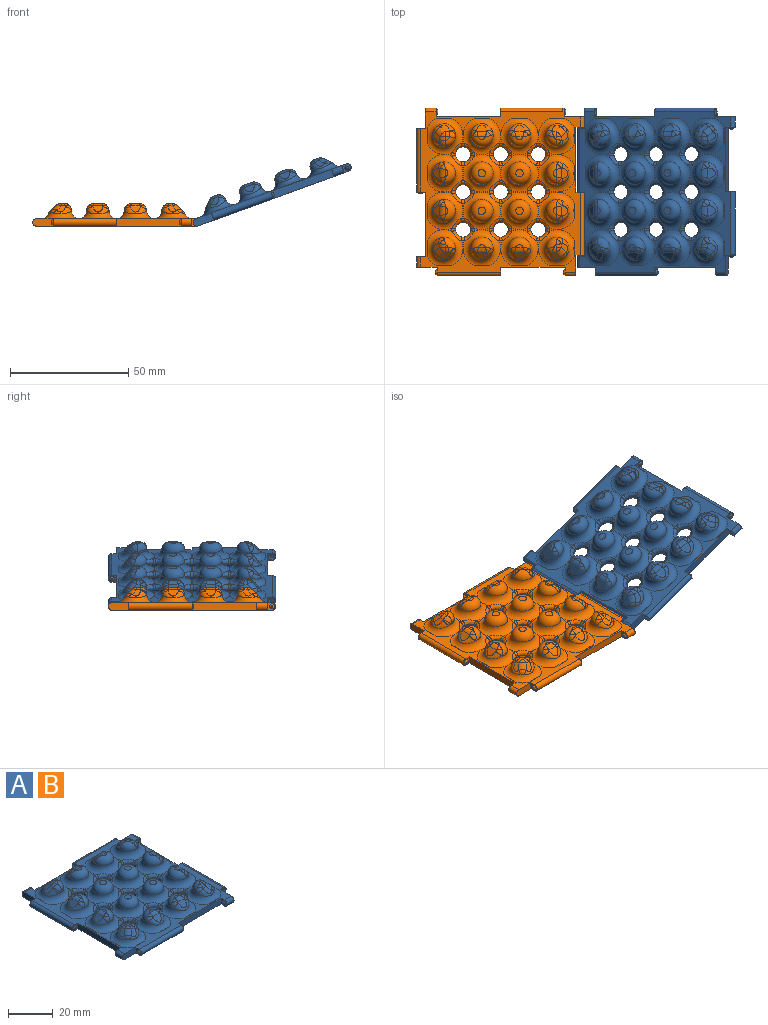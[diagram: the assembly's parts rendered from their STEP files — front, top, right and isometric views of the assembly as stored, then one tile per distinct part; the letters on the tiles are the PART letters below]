
ASSEMBLY  parts=2 mates=1
PART A: 345 faces, bbox 70.9x70.9x9.6 mm
  f0: cylinder r=3.17mm len=2.69mm, axis (0,0,-1), area 0mm2, adj f1,f344
  f1: bspline ~4.93x4.93mm, area 10.2mm2, adj f0,f2,f344
  f2: torus R=7.94mm, axis (0,0,1), area 169.6mm2, adj f1,f3,f5,f334,f335,f336,f337,f338
  f3: torus R=1.59mm, axis (0,0,1), area 113.1mm2, adj f2,f4
  f4: plane 3.18x3.18mm, normal (0,0,1), area 7.9mm2, adj f3
  f5: plane 3.22x1.37mm, normal (0,0,1), area 1.4mm2, adj f2,f6,f331
  f6: torus R=4.76mm, axis (0,0,1), area 69.6mm2, adj f5,f7,f8,f323,f324,f325,f326,f327
  f7: cylinder r=3.17mm len=2.69mm, axis (0,0,-1), area 0mm2, adj f6,f330
  f8: plane 67.68x67.68mm, normal (0,0,-1), area 3651.9mm2, adj f6,f9,f256,f259,f260,f261,f264,f265
  f9: plane 27.25x3.18mm, normal (1,0,0), area 86.5mm2, adj f8,f10,f256,f305
  f10: plane 67.68x67.68mm, normal (0,0,1), area 689.2mm2, adj f9,f11,f12,f13,f63,f64,f79,f80
  f11: plane 6.54x0.11mm, normal (0,-0.71,0.71), area 0.5mm2, adj f10,f237
  f12: plane 6.54x0.11mm, normal (0,-0.71,0.71), area 0.5mm2, adj f10,f13
  f13: torus R=7.94mm, axis (0,0,1), area 164.4mm2, adj f10,f12,f14,f47,f49,f50,f58,f59
  f14: plane 3.22x1.37mm, normal (0,0,1), area 1.4mm2, adj f13,f15,f320
  f15: torus R=7.94mm, axis (0,0,1), area 169.6mm2, adj f14,f16,f18,f36,f38,f40,f41,f42
  f16: torus R=1.59mm, axis (0,0,1), area 113.1mm2, adj f15,f17
  f17: plane 3.18x3.18mm, normal (0,0,1), area 7.9mm2, adj f16
  f18: plane 3.22x1.37mm, normal (0,0,1), area 1.4mm2, adj f15,f19,f314
  f19: torus R=7.94mm, axis (0,0,1), area 169.6mm2, adj f18,f20,f22,f23,f25,f26,f27,f29
  f20: torus R=1.59mm, axis (0,0,1), area 113.1mm2, adj f19,f21
  f21: plane 3.18x3.18mm, normal (0,0,1), area 7.9mm2, adj f20
  f22: plane 3.22x1.37mm, normal (0,0,1), area 1.4mm2, adj f19,f101,f311
  f23: bspline ~4.93x4.93mm, area 10.2mm2, adj f19,f24,f311
  f24: cylinder r=3.17mm len=2.69mm, axis (0,0,-1), area 0mm2, adj f23,f311
  f25: plane 3.22x1.37mm, normal (0,0,1), area 1.4mm2, adj f19,f311,f331
  f26: plane 3.22x1.37mm, normal (0,0,1), area 1.4mm2, adj f19,f314,f331
  f27: bspline ~4.93x4.93mm, area 10.2mm2, adj f19,f28,f314
  f28: cylinder r=3.17mm len=2.69mm, axis (0,0,-1), area 0mm2, adj f27,f314
  f29: bspline ~4.93x4.93mm, area 10.2mm2, adj f19,f30,f321
  f30: cylinder r=3.17mm len=2.69mm, axis (0,0,-1), area 0mm2, adj f29,f321
  f31: plane 3.22x1.37mm, normal (0,0,1), area 1.4mm2, adj f19,f64,f321
  f32: plane 3.22x1.37mm, normal (0,0,1), area 1.4mm2, adj f19,f64,f322
  f33: bspline ~4.93x4.93mm, area 10.2mm2, adj f19,f34,f322
  f34: cylinder r=3.17mm len=2.69mm, axis (0,0,-1), area 0mm2, adj f33,f322
  f35: plane 3.22x1.37mm, normal (0,0,1), area 1.4mm2, adj f19,f101,f322
  f36: bspline ~4.93x4.93mm, area 10.2mm2, adj f15,f37,f314
  f37: cylinder r=3.17mm len=2.69mm, axis (0,0,-1), area 0mm2, adj f36,f314
  f38: bspline ~4.93x4.93mm, area 10.2mm2, adj f15,f39,f318
  f39: cylinder r=3.17mm len=2.69mm, axis (0,0,-1), area 0mm2, adj f38,f318
  f40: plane 3.22x1.37mm, normal (0,0,1), area 1.4mm2, adj f15,f222,f318
  f41: plane 3.22x1.37mm, normal (0,0,1), area 1.4mm2, adj f15,f222,f320
  f42: bspline ~4.93x4.93mm, area 10.2mm2, adj f15,f43,f320
  f43: cylinder r=3.17mm len=2.69mm, axis (0,0,-1), area 0mm2, adj f42,f320
  f44: bspline ~4.93x4.93mm, area 10.2mm2, adj f15,f45,f321
  f45: cylinder r=3.17mm len=2.69mm, axis (0,0,-1), area 0mm2, adj f44,f321
  f46: plane 3.22x1.37mm, normal (0,0,1), area 1.4mm2, adj f15,f19,f321
  f47: bspline ~4.93x4.93mm, area 10.2mm2, adj f13,f48,f320
  f48: cylinder r=3.17mm len=2.69mm, axis (0,0,-1), area 0mm2, adj f47,f320
  f49: plane 3.22x1.37mm, normal (0,0,1), area 1.4mm2, adj f13,f237,f320
  f50: bspline ~9.97x5.14mm, area 21.5mm2, adj f13,f51,f56,f57
  f51: plane 4.37x2.65mm, normal (0,-0.71,0.71), area 12.6mm2, adj f50,f52,f56,f57
  f52: cylinder r=3.17mm len=4.07mm, axis (1,0,0), area 8.9mm2, adj f51,f53,f54,f55
  f53: bspline ~2.68x2.63mm, area 3.3mm2, adj f52,f57,f58
  f54: plane 3.06x1.16mm, normal (0,0,1), area 2.6mm2, adj f52,f58
  f55: bspline ~2.68x2.63mm, area 3.3mm2, adj f52,f56,f58
  f56: bspline ~3.74x3.12mm, area 5.3mm2, adj f50,f51,f55,f58
  f57: bspline ~3.74x3.12mm, area 5.3mm2, adj f50,f51,f53,f58
  f58: torus R=1.59mm, axis (0,0,1), area 57.5mm2, adj f13,f53,f54,f55,f56,f57
  f59: plane 3.22x1.37mm, normal (0,0,1), area 1.4mm2, adj f13,f64,f321
  f60: bspline ~4.93x4.93mm, area 10.2mm2, adj f13,f61,f321
  f61: cylinder r=3.17mm len=2.69mm, axis (0,0,-1), area 0mm2, adj f60,f321
  f62: plane 3.22x1.37mm, normal (0,0,1), area 1.4mm2, adj f13,f15,f321
  f63: plane 6.54x0.11mm, normal (0,-0.71,0.71), area 0.5mm2, adj f10,f64
  f64: torus R=7.94mm, axis (0,0,1), area 164.4mm2, adj f10,f31,f32,f59,f63,f65,f67,f75
  f65: bspline ~4.93x4.93mm, area 10.2mm2, adj f64,f66,f321
  f66: cylinder r=3.17mm len=2.69mm, axis (0,0,-1), area 0mm2, adj f65,f321
  f67: bspline ~9.7x5.14mm, area 21.5mm2, adj f64,f68,f73,f74
  f68: plane 4.37x2.65mm, normal (0,-0.71,0.71), area 12.6mm2, adj f67,f69,f73,f74
  f69: cylinder r=3.17mm len=4.07mm, axis (1,0,0), area 8.9mm2, adj f68,f70,f71,f72
  f70: bspline ~2.68x2.63mm, area 3.3mm2, adj f69,f74,f75
  f71: plane 3.06x1.16mm, normal (0,0,1), area 2.6mm2, adj f69,f75
  f72: bspline ~2.68x2.63mm, area 3.3mm2, adj f69,f73,f75
  f73: bspline ~3.74x3.12mm, area 5.3mm2, adj f67,f68,f72,f75
  f74: bspline ~3.74x3.12mm, area 5.3mm2, adj f67,f68,f70,f75
  f75: torus R=1.59mm, axis (0,0,1), area 57.5mm2, adj f64,f70,f71,f72,f73,f74
  f76: plane 3.22x1.37mm, normal (0,0,1), area 1.4mm2, adj f64,f81,f322
  f77: bspline ~4.93x4.93mm, area 10.2mm2, adj f64,f78,f322
  f78: cylinder r=3.17mm len=2.69mm, axis (0,0,-1), area 0mm2, adj f77,f322
  f79: plane 6.54x0.11mm, normal (0,-0.71,0.71), area 0.5mm2, adj f10,f81
  f80: plane 6.55x0.11mm, normal (0.71,0,0.71), area 0.5mm2, adj f10,f81
  f81: torus R=7.94mm, axis (0,0,1), area 157mm2, adj f10,f76,f79,f80,f82,f83,f85,f97
  f82: plane 3.22x1.37mm, normal (0,0,1), area 1.4mm2, adj f81,f101,f322
  f83: bspline ~4.93x4.93mm, area 10.2mm2, adj f81,f84,f322
  f84: cylinder r=3.17mm len=2.69mm, axis (0,0,-1), area 0mm2, adj f83,f322
  f85: bspline ~3.03x3.01mm, area 4.3mm2, adj f81,f86,f97,f99
  f86: cylinder r=3.17mm len=4.14mm, axis (-0.58,0.58,0.58), area 10.9mm2, adj f85,f87,f95,f96
  f87: sphere r=3.17mm, area 3.4mm2, adj f86,f88,f92
  f88: cylinder r=3.17mm len=2.25mm, axis (0,1,0), area 3.4mm2, adj f87,f89,f90,f95
  f89: plane 1.1x1.09mm, normal (0,0,1), area 0.8mm2, adj f88,f92,f98
  f90: bspline ~2.68x2.63mm, area 3.3mm2, adj f88,f91,f98
  f91: bspline ~3.74x3.12mm, area 5.3mm2, adj f90,f95,f98,f99
  f92: cylinder r=3.17mm len=2.25mm, axis (1,0,0), area 3.4mm2, adj f87,f89,f93,f96
  f93: bspline ~2.68x2.63mm, area 3.3mm2, adj f92,f94,f98
  f94: bspline ~3.74x3.12mm, area 5.3mm2, adj f93,f96,f97,f98
  f95: plane 3.65x2.65mm, normal (0.71,0,0.71), area 8.7mm2, adj f86,f88,f91,f99
  f96: plane 3.65x2.64mm, normal (0,-0.71,0.71), area 8.7mm2, adj f86,f92,f94,f97
  f97: bspline ~8.52x5.14mm, area 14.1mm2, adj f81,f85,f94,f96
  f98: torus R=1.59mm, axis (0,0,1), area 29.2mm2, adj f81,f89,f90,f91,f93,f94
  f99: bspline ~8.53x5.15mm, area 14.2mm2, adj f81,f85,f91,f95
  f100: plane 6.55x0.11mm, normal (0.71,0,0.71), area 0.5mm2, adj f10,f101
  f101: torus R=7.94mm, axis (0,0,1), area 164.4mm2, adj f10,f22,f35,f82,f100,f102,f103,f105
  f102: plane 3.22x1.37mm, normal (0,0,1), area 1.4mm2, adj f101,f117,f311
  f103: bspline ~4.93x4.93mm, area 10.2mm2, adj f101,f104,f311
  f104: cylinder r=3.17mm len=2.69mm, axis (0,0,-1), area 0mm2, adj f103,f311
  f105: bspline ~4.93x4.93mm, area 10.2mm2, adj f101,f106,f322
  f106: cylinder r=3.17mm len=2.69mm, axis (0,0,-1), area 0mm2, adj f105,f322
  f107: torus R=1.59mm, axis (0,0,1), area 57.4mm2, adj f101,f108,f111,f112,f113,f114
  f108: bspline ~2.68x2.63mm, area 3.3mm2, adj f107,f109,f111
  f109: cylinder r=3.17mm len=4.07mm, axis (0,1,0), area 8.9mm2, adj f108,f110,f113,f114
  f110: plane 4.37x2.65mm, normal (0.71,0,0.71), area 12.6mm2, adj f109,f111,f112,f115
  f111: bspline ~3.74x3.12mm, area 5.3mm2, adj f107,f108,f110,f115
  f112: bspline ~3.74x3.12mm, area 5.3mm2, adj f107,f110,f113,f115
  f113: bspline ~2.68x2.63mm, area 3.3mm2, adj f107,f109,f112
  f114: plane 3.05x1.15mm, normal (0,0,1), area 2.6mm2, adj f107,f109
  f115: bspline ~9.98x5.15mm, area 21.5mm2, adj f101,f110,f111,f112
  f116: plane 6.55x0.11mm, normal (0.71,0,0.71), area 0.5mm2, adj f10,f117
  f117: torus R=7.94mm, axis (0,0,1), area 164.4mm2, adj f10,f102,f116,f118,f119,f121,f122,f123
  f118: plane 3.22x1.37mm, normal (0,0,1), area 1.4mm2, adj f117,f136,f308
  f119: bspline ~4.93x4.93mm, area 10.2mm2, adj f117,f120,f308
  f120: cylinder r=3.17mm len=2.69mm, axis (0,0,-1), area 0mm2, adj f119,f308
  f121: plane 3.22x1.37mm, normal (0,0,1), area 1.4mm2, adj f117,f308,f331
  f122: plane 3.22x1.37mm, normal (0,0,1), area 1.4mm2, adj f117,f311,f331
  f123: bspline ~4.93x4.93mm, area 10.2mm2, adj f117,f124,f311
  f124: cylinder r=3.17mm len=2.69mm, axis (0,0,-1), area 0mm2, adj f123,f311
  f125: torus R=1.59mm, axis (0,0,1), area 57.4mm2, adj f117,f126,f129,f130,f131,f132
  f126: bspline ~2.68x2.63mm, area 3.3mm2, adj f125,f127,f129
  f127: cylinder r=3.17mm len=4.07mm, axis (0,1,0), area 8.9mm2, adj f126,f128,f131,f132
  f128: plane 4.37x2.65mm, normal (0.71,0,0.71), area 12.6mm2, adj f127,f129,f130,f133
  f129: bspline ~3.62x3.03mm, area 5.3mm2, adj f125,f126,f128,f133
  f130: bspline ~3.74x3.12mm, area 5.3mm2, adj f125,f128,f131,f133
  f131: bspline ~2.68x2.63mm, area 3.3mm2, adj f125,f127,f130
  f132: plane 3.05x1.15mm, normal (0,0,1), area 2.6mm2, adj f125,f127
  f133: bspline ~9.98x5.15mm, area 21.5mm2, adj f117,f128,f129,f130
  f134: plane 6.55x0.11mm, normal (0.71,0,0.71), area 0.5mm2, adj f10,f136
  f135: plane 6.54x0.11mm, normal (0,0.71,0.71), area 0.5mm2, adj f10,f136
  f136: torus R=7.94mm, axis (0,0,1), area 157.1mm2, adj f10,f118,f134,f135,f137,f138,f140,f152
  f137: plane 3.22x1.37mm, normal (0,0,1), area 1.4mm2, adj f136,f156,f308
  f138: bspline ~4.93x4.93mm, area 10.2mm2, adj f136,f139,f308
  f139: cylinder r=3.17mm len=2.69mm, axis (0,0,-1), area 0mm2, adj f138,f308
  f140: torus R=1.59mm, axis (0,0,1), area 29.2mm2, adj f136,f141,f148,f149,f150,f151
  f141: bspline ~3.74x3.12mm, area 5.3mm2, adj f140,f142,f148,f152
  f142: plane 3.65x2.65mm, normal (0,0.71,0.71), area 8.7mm2, adj f141,f143,f147,f152
  f143: cylinder r=3.17mm len=2.25mm, axis (-1,0,0), area 3.4mm2, adj f142,f144,f148,f149
  f144: sphere r=3.17mm, area 3.4mm2, adj f143,f145,f147
  f145: cylinder r=3.17mm len=2.25mm, axis (0,1,0), area 3.4mm2, adj f144,f146,f149,f150
  f146: plane 3.65x2.65mm, normal (0.71,0,0.71), area 8.7mm2, adj f145,f147,f151,f154
  f147: cylinder r=3.17mm len=4.14mm, axis (0.58,0.58,-0.58), area 10.9mm2, adj f142,f144,f146,f153
  f148: bspline ~2.68x2.63mm, area 3.3mm2, adj f140,f141,f143
  f149: plane 1.1x1.09mm, normal (0,0,1), area 0.8mm2, adj f140,f143,f145
  f150: bspline ~2.68x2.63mm, area 3.3mm2, adj f140,f145,f151
  f151: bspline ~3.74x3.12mm, area 5.3mm2, adj f140,f146,f150,f154
  f152: bspline ~8.52x5.14mm, area 14.1mm2, adj f136,f141,f142,f153
  f153: bspline ~3.04x3.01mm, area 4.3mm2, adj f136,f147,f152,f154
  f154: bspline ~8.11x5.15mm, area 14.2mm2, adj f136,f146,f151,f153
  f155: plane 6.54x0.11mm, normal (0,0.71,0.71), area 0.5mm2, adj f10,f156
  f156: torus R=7.94mm, axis (0,0,1), area 164.4mm2, adj f10,f137,f155,f157,f158,f160,f168,f323
  f157: plane 3.22x1.37mm, normal (0,0,1), area 1.4mm2, adj f156,f308,f331
  f158: bspline ~4.93x4.93mm, area 10.2mm2, adj f156,f159,f308
  f159: cylinder r=3.17mm len=2.69mm, axis (0,0,-1), area 0mm2, adj f158,f308
  f160: bspline ~9.7x5.14mm, area 21.5mm2, adj f156,f161,f166,f167
  f161: bspline ~3.74x3.12mm, area 5.3mm2, adj f160,f162,f166,f168
  f162: bspline ~2.68x2.63mm, area 3.3mm2, adj f161,f163,f168
  f163: cylinder r=3.17mm len=4.07mm, axis (-1,0,0), area 8.9mm2, adj f162,f164,f165,f166
  f164: bspline ~2.68x2.63mm, area 3.3mm2, adj f163,f167,f168
  f165: plane 3.06x1.16mm, normal (0,0,1), area 2.6mm2, adj f163,f168
  f166: plane 4.37x2.65mm, normal (0,0.71,0.71), area 12.6mm2, adj f160,f161,f163,f167
  f167: bspline ~3.74x3.12mm, area 5.3mm2, adj f160,f164,f166,f168
  f168: torus R=1.59mm, axis (0,0,1), area 57.5mm2, adj f156,f161,f162,f164,f165,f167
  f169: plane 6.54x0.11mm, normal (0,0.71,0.71), area 0.5mm2, adj f10,f170
  f170: torus R=7.94mm, axis (0,0,1), area 164.4mm2, adj f10,f169,f171,f179,f180,f181,f328,f329
  f171: bspline ~9.7x5.14mm, area 21.5mm2, adj f170,f172,f177,f178
  f172: bspline ~3.74x3.12mm, area 5.3mm2, adj f171,f173,f177,f179
  f173: bspline ~2.68x2.63mm, area 3.3mm2, adj f172,f174,f179
  f174: cylinder r=3.17mm len=4.07mm, axis (-1,0,0), area 8.9mm2, adj f173,f175,f176,f177
  f175: bspline ~2.68x2.63mm, area 3.3mm2, adj f174,f178,f179
  f176: plane 3.06x1.16mm, normal (0,0,1), area 2.6mm2, adj f174,f179
  f177: plane 4.37x2.65mm, normal (0,0.71,0.71), area 12.6mm2, adj f171,f172,f174,f178
  f178: bspline ~3.74x3.12mm, area 5.3mm2, adj f171,f175,f177,f179
  f179: torus R=1.59mm, axis (0,0,1), area 57.5mm2, adj f170,f172,f173,f175,f176,f178
  f180: plane 3.22x1.37mm, normal (0,0,1), area 1.4mm2, adj f170,f185,f344
  f181: bspline ~4.93x4.93mm, area 10.2mm2, adj f170,f182,f344
  f182: cylinder r=3.17mm len=2.69mm, axis (0,0,-1), area 0mm2, adj f181,f344
  f183: plane 6.54x0.11mm, normal (0,0.71,0.71), area 0.5mm2, adj f10,f185
  f184: plane 6.55x0.11mm, normal (-0.71,0,0.71), area 0.5mm2, adj f10,f185
  f185: torus R=7.94mm, axis (0,0,1), area 157mm2, adj f10,f180,f183,f184,f186,f187,f189,f202
  f186: plane 3.22x1.37mm, normal (0,0,1), area 1.4mm2, adj f185,f206,f344
  f187: bspline ~4.93x4.93mm, area 10.2mm2, adj f185,f188,f344
  f188: cylinder r=3.17mm len=2.69mm, axis (0,0,-1), area 0mm2, adj f187,f344
  f189: bspline ~8.53x5.15mm, area 14.2mm2, adj f185,f190,f201,f202
  f190: plane 3.69x2.65mm, normal (-0.71,0,0.71), area 8.8mm2, adj f189,f191,f200,f201
  f191: cylinder r=3.17mm len=2.25mm, axis (0,-1,0), area 4.4mm2, adj f190,f192,f198,f199
  f192: sphere r=3.17mm, area 3.4mm2, adj f191,f193,f200
  f193: cylinder r=3.17mm len=2.25mm, axis (-1,0,0), area 4.4mm2, adj f192,f194,f196,f198
  f194: plane 3.69x2.65mm, normal (0,0.71,0.71), area 8.8mm2, adj f193,f195,f200,f203
  f195: bspline ~2.92x2.69mm, area 3.3mm2, adj f194,f196,f203,f204
  f196: bspline ~4.05x2.87mm, area 8.4mm2, adj f193,f195,f197,f204
  f197: torus R=2.22mm, axis (0,0,1), area 18.1mm2, adj f196,f198,f199,f204
  f198: plane 1.75x1.75mm, normal (0,0,1), area 2.2mm2, adj f191,f193,f197
  f199: bspline ~4.05x2.87mm, area 8.4mm2, adj f191,f197,f201,f204
  f200: cylinder r=3.17mm len=4.14mm, axis (0.58,-0.58,0.58), area 10.9mm2, adj f190,f192,f194,f202
  f201: bspline ~2.92x2.69mm, area 3.3mm2, adj f189,f190,f199,f204
  f202: bspline ~3.03x3.01mm, area 4.3mm2, adj f185,f189,f200,f203
  f203: bspline ~8.52x5.14mm, area 14.1mm2, adj f185,f194,f195,f202
  f204: cylinder r=4.76mm len=5.76mm, axis (0,0,-1), area 5mm2, adj f185,f195,f196,f197,f199,f201
  f205: plane 6.55x0.11mm, normal (-0.71,0,0.71), area 0.5mm2, adj f10,f206
  f206: torus R=7.94mm, axis (0,0,1), area 164.3mm2, adj f10,f186,f205,f207,f208,f210,f218,f219
  f207: plane 3.22x1.37mm, normal (0,0,1), area 1.4mm2, adj f206,f222,f318
  f208: bspline ~4.93x4.93mm, area 10.2mm2, adj f206,f209,f318
  f209: cylinder r=3.17mm len=2.69mm, axis (0,0,-1), area 0mm2, adj f208,f318
  f210: bspline ~9.98x5.15mm, area 21.5mm2, adj f206,f211,f216,f217
  f211: plane 4.37x2.65mm, normal (-0.71,0,0.71), area 12.6mm2, adj f210,f212,f216,f217
  f212: cylinder r=3.17mm len=4.07mm, axis (0,-1,0), area 8.9mm2, adj f211,f213,f214,f215
  f213: bspline ~2.68x2.63mm, area 3.3mm2, adj f212,f217,f218
  f214: plane 3.05x1.15mm, normal (0,0,1), area 2.6mm2, adj f212,f218
  f215: bspline ~2.68x2.63mm, area 3.3mm2, adj f212,f216,f218
  f216: bspline ~3.74x3.12mm, area 5.3mm2, adj f210,f211,f215,f218
  f217: bspline ~3.74x3.12mm, area 5.3mm2, adj f210,f211,f213,f218
  f218: torus R=1.59mm, axis (0,0,1), area 57.4mm2, adj f206,f213,f214,f215,f216,f217
  f219: bspline ~4.93x4.93mm, area 10.2mm2, adj f206,f220,f344
  f220: cylinder r=3.17mm len=2.69mm, axis (0,0,-1), area 0mm2, adj f219,f344
  f221: plane 6.55x0.11mm, normal (-0.71,0,0.71), area 0.5mm2, adj f10,f222
  f222: torus R=7.94mm, axis (0,0,1), area 164.3mm2, adj f10,f40,f41,f207,f221,f223,f231,f232
  f223: bspline ~9.98x5.15mm, area 21.5mm2, adj f222,f224,f229,f230
  f224: plane 4.37x2.65mm, normal (-0.71,0,0.71), area 12.6mm2, adj f223,f225,f229,f230
  f225: cylinder r=3.17mm len=4.07mm, axis (0,-1,0), area 8.9mm2, adj f224,f226,f227,f228
  f226: bspline ~2.68x2.63mm, area 3.3mm2, adj f225,f230,f231
  f227: plane 3.05x1.15mm, normal (0,0,1), area 2.6mm2, adj f225,f231
  f228: bspline ~2.68x2.63mm, area 3.3mm2, adj f225,f229,f231
  f229: bspline ~3.74x3.12mm, area 5.3mm2, adj f223,f224,f228,f231
  f230: bspline ~3.74x3.12mm, area 5.3mm2, adj f223,f224,f226,f231
  f231: torus R=1.59mm, axis (0,0,1), area 57.4mm2, adj f222,f226,f227,f228,f229,f230
  f232: bspline ~4.93x4.93mm, area 10.2mm2, adj f222,f233,f318
  f233: cylinder r=3.17mm len=2.69mm, axis (0,0,-1), area 0mm2, adj f232,f318
  f234: plane 3.22x1.37mm, normal (0,0,1), area 1.4mm2, adj f222,f237,f320
  f235: bspline ~4.93x4.93mm, area 10.2mm2, adj f222,f236,f320
  f236: cylinder r=3.17mm len=2.69mm, axis (0,0,-1), area 0mm2, adj f235,f320
  f237: torus R=7.94mm, axis (0,0,1), area 157mm2, adj f10,f11,f49,f234,f238,f250,f251,f252
  f238: bspline ~8.26x4.29mm, area 14.1mm2, adj f237,f239,f249,f250
  f239: plane 3.65x2.65mm, normal (0,-0.71,0.71), area 8.7mm2, adj f238,f240,f247,f249
  f240: cylinder r=3.17mm len=4.14mm, axis (-0.58,-0.58,-0.58), area 10.9mm2, adj f239,f241,f246,f250
  f241: sphere r=3.17mm, area 3.4mm2, adj f240,f242,f247
  f242: cylinder r=3.17mm len=2.25mm, axis (0,-1,0), area 3.4mm2, adj f241,f243,f245,f246
  f243: bspline ~2.68x2.63mm, area 3.3mm2, adj f242,f244,f252
  f244: bspline ~3.74x3.12mm, area 5.3mm2, adj f243,f246,f251,f252
  f245: plane 1.1x1.09mm, normal (0,0,1), area 0.8mm2, adj f242,f247,f252
  f246: plane 3.65x2.65mm, normal (-0.71,0,0.71), area 8.7mm2, adj f240,f242,f244,f251
  f247: cylinder r=3.17mm len=2.25mm, axis (1,0,0), area 3.4mm2, adj f239,f241,f245,f248
  f248: bspline ~2.68x2.63mm, area 3.3mm2, adj f247,f249,f252
  f249: bspline ~3.74x3.12mm, area 5.3mm2, adj f238,f239,f248,f252
  f250: bspline ~3.04x3.01mm, area 4.3mm2, adj f237,f238,f240,f251
  f251: bspline ~8.26x4.3mm, area 14.2mm2, adj f237,f244,f246,f250
  f252: torus R=1.59mm, axis (0,0,1), area 29.2mm2, adj f237,f243,f244,f245,f248,f249
  f253: bspline ~4.93x4.93mm, area 10.2mm2, adj f237,f254,f320
  f254: cylinder r=3.17mm len=2.69mm, axis (0,0,-1), area 0mm2, adj f253,f320
  f255: plane 6.55x0.11mm, normal (-0.71,0,0.71), area 0.5mm2, adj f10,f237
  f256: plane 3.68x3.18mm, normal (0,-1,0), area 4.1mm2, adj f8,f9,f10,f257,f259
  f257: torus R=0.69mm, axis (0,-1,0), area 8.6mm2, adj f256,f258
  f258: plane 1.38x1.38mm, normal (0,-1,0), area 1.5mm2, adj f257
  f259: cylinder r=1.59mm len=4.5mm, axis (0,-1,0), area 22.4mm2, adj f8,f10,f256,f260
  f260: plane 8.68x3.18mm, normal (0,1,0), area 26.5mm2, adj f8,f10,f259,f261
  f261: plane 3.7x3.19mm, normal (1,0,0), area 6.9mm2, adj f8,f10,f260,f262,f264
  f262: torus R=0.34mm, axis (1,0,0), area 6mm2, adj f261,f263
  f263: plane 0.68x0.68mm, normal (1,0,0), area 0.4mm2, adj f262
  f264: cylinder r=1.59mm len=3.18mm, axis (-1,-0.01,0), area 2.5mm2, adj f8,f10,f261,f265
  f265: cylinder r=1.59mm len=26.25mm, axis (-1,0,0), area 130.9mm2, adj f8,f10,f264,f266
  f266: plane 3.68x3.18mm, normal (-1,0,0), area 4.1mm2, adj f8,f10,f265,f267,f269
  f267: torus R=0.69mm, axis (-1,0,0), area 8.6mm2, adj f266,f268
  f268: plane 1.38x1.38mm, normal (-1,0,0), area 1.5mm2, adj f267
  f269: plane 27.25x3.18mm, normal (0,1,0), area 86.5mm2, adj f8,f10,f266,f270
  f270: plane 3.68x3.18mm, normal (1,0,0), area 6.9mm2, adj f8,f10,f269,f271,f273
  f271: torus R=0.34mm, axis (1,0,0), area 6mm2, adj f270,f272
  f272: plane 0.68x0.68mm, normal (1,0,0), area 0.4mm2, adj f271
  f273: cylinder r=1.59mm len=4.5mm, axis (1,0,0), area 22.4mm2, adj f8,f10,f270,f274
  f274: plane 8.68x3.18mm, normal (-1,0,0), area 26.5mm2, adj f8,f10,f273,f275
  f275: plane 3.68x3.18mm, normal (0,1,0), area 4.1mm2, adj f8,f10,f274,f276,f278
  f276: torus R=0.69mm, axis (0,1,0), area 8.6mm2, adj f275,f277
  f277: plane 1.38x1.38mm, normal (0,1,0), area 1.5mm2, adj f276
  f278: cylinder r=1.59mm len=26.75mm, axis (0,1,0), area 133.4mm2, adj f8,f10,f275,f279
  f279: plane 3.68x3.18mm, normal (0,-1,0), area 6.9mm2, adj f8,f10,f278,f280,f282
  f280: torus R=0.34mm, axis (0,-1,0), area 6mm2, adj f279,f281
  f281: plane 0.68x0.68mm, normal (0,-1,0), area 0.4mm2, adj f280
  f282: plane 27.25x3.18mm, normal (-1,0,0), area 86.5mm2, adj f8,f10,f279,f283
  f283: plane 3.68x3.18mm, normal (0,1,0), area 4.1mm2, adj f8,f10,f282,f284,f286
  f284: torus R=0.69mm, axis (0,1,0), area 8.6mm2, adj f283,f285
  f285: plane 1.38x1.38mm, normal (0,1,0), area 1.5mm2, adj f284
  f286: cylinder r=1.59mm len=4.5mm, axis (0,1,0), area 22.4mm2, adj f8,f10,f283,f287
  f287: plane 8.68x3.18mm, normal (0,-1,0), area 26.5mm2, adj f8,f10,f286,f288
  f288: plane 3.68x3.18mm, normal (-1,0,0), area 6.9mm2, adj f8,f10,f287,f289,f291
  f289: torus R=0.34mm, axis (-1,0,0), area 6mm2, adj f288,f290
  f290: plane 0.68x0.68mm, normal (-1,0,0), area 0.4mm2, adj f289
  f291: cylinder r=1.59mm len=26.75mm, axis (-1,0,0), area 133.4mm2, adj f8,f10,f288,f292
  f292: plane 3.68x3.18mm, normal (1,0,0), area 4.1mm2, adj f8,f10,f291,f293,f295
  f293: torus R=0.69mm, axis (1,0,0), area 8.6mm2, adj f292,f294
  f294: plane 1.38x1.38mm, normal (1,0,0), area 1.5mm2, adj f293
  f295: plane 27.25x3.18mm, normal (0,-1,0), area 86.5mm2, adj f8,f10,f292,f296
  f296: plane 3.68x3.18mm, normal (-1,0,0), area 6.9mm2, adj f8,f10,f295,f297,f299
  f297: torus R=0.34mm, axis (-1,0,0), area 6mm2, adj f296,f298
  f298: plane 0.68x0.68mm, normal (-1,0,0), area 0.4mm2, adj f297
  f299: cylinder r=1.59mm len=4.5mm, axis (-1,0,0), area 22.4mm2, adj f8,f10,f296,f300
  f300: plane 8.68x3.18mm, normal (1,0,0), area 26.5mm2, adj f8,f10,f299,f301
  f301: plane 3.68x3.18mm, normal (0,-1,0), area 4.1mm2, adj f8,f10,f300,f302,f304
  f302: torus R=0.69mm, axis (0,-1,0), area 8.6mm2, adj f301,f303
  f303: plane 1.38x1.38mm, normal (0,-1,0), area 1.5mm2, adj f302
  f304: cylinder r=1.59mm len=26.75mm, axis (0,-1,0), area 133.4mm2, adj f8,f10,f301,f305
  f305: plane 3.68x3.18mm, normal (0,1,0), area 6.9mm2, adj f8,f9,f10,f304,f306
  f306: torus R=0.34mm, axis (0,1,0), area 6mm2, adj f305,f307
  f307: plane 0.68x0.68mm, normal (0,1,0), area 0.4mm2, adj f306
  f308: torus R=4.76mm, axis (0,0,1), area 69.6mm2, adj f8,f118,f119,f120,f121,f137,f138,f139
  f309: cylinder r=3.17mm len=2.69mm, axis (0,0,-1), area 0mm2, adj f308,f310
  f310: bspline ~4.93x4.93mm, area 10.2mm2, adj f308,f309,f331
  f311: torus R=4.76mm, axis (0,0,1), area 69.6mm2, adj f8,f22,f23,f24,f25,f102,f103,f104
  f312: cylinder r=3.17mm len=2.69mm, axis (0,0,-1), area 0mm2, adj f311,f313
  f313: bspline ~4.93x4.93mm, area 10.2mm2, adj f311,f312,f331
  f314: torus R=4.76mm, axis (0,0,1), area 69.6mm2, adj f8,f18,f26,f27,f28,f36,f37,f315
  f315: cylinder r=3.17mm len=2.69mm, axis (0,0,-1), area 0mm2, adj f314,f317
  f316: cylinder r=3.17mm len=2.69mm, axis (0,0,-1), area 0mm2, adj f314,f342
  f317: bspline ~4.93x4.93mm, area 10.2mm2, adj f314,f315,f331
  f318: torus R=4.76mm, axis (0,0,1), area 69.6mm2, adj f8,f38,f39,f40,f207,f208,f209,f232
  f319: cylinder r=3.17mm len=2.69mm, axis (0,0,-1), area 0mm2, adj f318,f339
  f320: torus R=4.76mm, axis (0,0,1), area 69.6mm2, adj f8,f14,f41,f42,f43,f47,f48,f49
  f321: torus R=4.76mm, axis (0,0,1), area 69.6mm2, adj f8,f29,f30,f31,f44,f45,f46,f59
  f322: torus R=4.76mm, axis (0,0,1), area 69.6mm2, adj f8,f32,f33,f34,f35,f76,f77,f78
  f323: plane 3.22x1.37mm, normal (0,0,1), area 1.4mm2, adj f6,f156,f331
  f324: cylinder r=3.17mm len=2.69mm, axis (0,0,-1), area 0mm2, adj f6,f325
  f325: bspline ~4.93x4.93mm, area 10.2mm2, adj f6,f324,f331
  f326: cylinder r=3.17mm len=2.69mm, axis (0,0,-1), area 0mm2, adj f6,f334
  f327: cylinder r=3.17mm len=2.69mm, axis (0,0,-1), area 0mm2, adj f6,f328
  f328: bspline ~4.93x4.93mm, area 10.2mm2, adj f6,f170,f327
  f329: plane 3.22x1.37mm, normal (0,0,1), area 1.4mm2, adj f6,f156,f170
  f330: bspline ~4.93x4.93mm, area 10.2mm2, adj f6,f7,f156
  f331: torus R=7.94mm, axis (0,0,1), area 169.6mm2, adj f5,f25,f26,f121,f122,f157,f310,f313
  f332: torus R=1.59mm, axis (0,0,1), area 113.1mm2, adj f331,f333
  f333: plane 3.18x3.18mm, normal (0,0,1), area 7.9mm2, adj f332
  f334: bspline ~4.93x4.93mm, area 10.2mm2, adj f2,f6,f326
  f335: plane 3.22x1.37mm, normal (0,0,1), area 1.4mm2, adj f2,f6,f170
  f336: plane 3.22x1.37mm, normal (0,0,1), area 1.4mm2, adj f2,f170,f344
  f337: plane 3.22x1.37mm, normal (0,0,1), area 1.4mm2, adj f2,f206,f344
  f338: plane 3.22x1.37mm, normal (0,0,1), area 1.4mm2, adj f2,f206,f318
  f339: bspline ~4.93x4.93mm, area 10.2mm2, adj f2,f318,f319
  f340: plane 3.22x1.37mm, normal (0,0,1), area 1.4mm2, adj f2,f15,f318
  f341: plane 3.22x1.37mm, normal (0,0,1), area 1.4mm2, adj f2,f15,f314
  f342: bspline ~4.93x4.93mm, area 10.2mm2, adj f2,f314,f316
  f343: plane 3.22x1.37mm, normal (0,0,1), area 1.4mm2, adj f2,f314,f331
  f344: torus R=4.76mm, axis (0,0,1), area 69.6mm2, adj f0,f1,f8,f180,f181,f182,f186,f187
PART B: same geometry as A
PLACE A rot(axis=(0.17,-0.17,-0.97),91.7deg) t=(49.75,-3.52,11.9)mm
PLACE B t=(-16.42,-3.52,0.23)mm
MATE revolute A.f289 <-> B.f257  axis (0,-1,0) through (17.41,-2.77,1.82)mm
